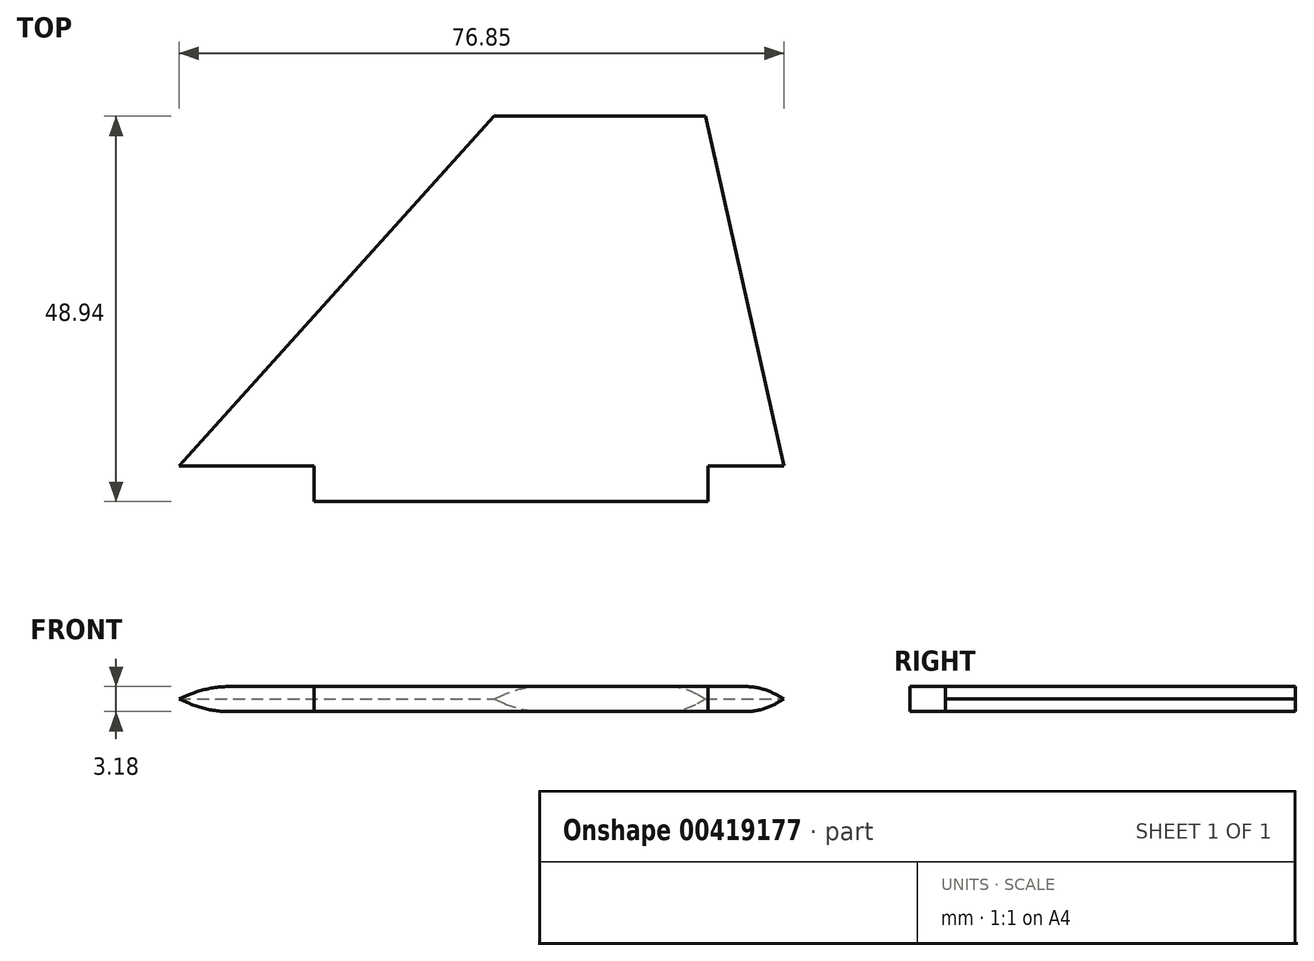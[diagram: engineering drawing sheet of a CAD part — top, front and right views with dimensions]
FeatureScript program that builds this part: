
annotation { "Feature Type Name" : "Feature", "Feature Type Description" : "" }
export const myFeature = defineFeature(function(context is Context, id is Id, definition is map)
    precondition{}
    {
        {
            var Q0;
            Q0=qCreatedBy(makeId("Top.planeOp"),FACE);
            var sketch = newSketch(context, id + "F0", { "sketchPlane" : qUnion([Q0])});
            skLineSegment(sketch, "E0", {"start": v(0, 0) * mm, "end": v(80, 0) * mm});
            skLineSegment(sketch, "E1", {"start": v(80, 0) * mm, "end": v(70, 44.44) * mm});
            skLineSegment(sketch, "E2", {"start": v(70, 44.44) * mm, "end": v(40, 44.44) * mm});
            skLineSegment(sketch, "E3", {"start": v(40, 44.44) * mm, "end": v(0, 0) * mm});
            skLineSegment(sketch, "E4", {"start": v(80, 0) * mm, "end": v(70, 0) * mm});
            skLineSegment(sketch, "E5", {"start": v(70, 0) * mm, "end": v(70, -4.5) * mm});
            skLineSegment(sketch, "E6", {"start": v(70, -4.5) * mm, "end": v(20, -4.5) * mm});
            skLineSegment(sketch, "E7", {"start": v(20, -4.5) * mm, "end": v(20, 0) * mm});
            skLineSegment(sketch, "E8", {"start": v(20, 0) * mm, "end": v(70, 0) * mm});
            skSolve(sketch);
        }
        {
            var Q0;
            Q0 = qSketchRegion(id + "F0", true);
            extrude(context, id + "F1", {"entities" : qUnion([Q0]), "endBound" : BoundingType.SYMMETRIC, "depth" : 3.17 * mm});
        }
        {
            var Q0;
            Q0=makeQuery(id+"F1.opExtrude","CAP_EDGE",EDGE,{"disambiguationData":[OSD([sQuery(id+"F0.wireOp",EDGE,"E3")])],"isStart":true});
            var Q1;
            Q1=makeQuery(id+"F1.opExtrude","CAP_EDGE",EDGE,{"disambiguationData":[OSD([sQuery(id+"F0.wireOp",EDGE,"E3")])],"isStart":false});
            chamfer(context, id + "F2", {"entities" : qUnion([Q0, Q1]), "chamferType" : ChamferType.OFFSET_ANGLE, "width" : 2.8 * mm, "oppositeDirection" : false, "angle" : 60 * degree, "tangentPropagation" : true});
        }
        {
            var Q0;
            Q0=makeQuery(id+"F1.opExtrude","CAP_EDGE",EDGE,{"disambiguationData":[OSD([sQuery(id+"F0.wireOp",EDGE,"E1")])],"isStart":true});
            var Q1;
            Q1=makeQuery(id+"F1.opExtrude","CAP_EDGE",EDGE,{"disambiguationData":[OSD([sQuery(id+"F0.wireOp",EDGE,"E1")])],"isStart":false});
            chamfer(context, id + "F3", {"entities" : qUnion([Q0, Q1]), "chamferType" : ChamferType.OFFSET_ANGLE, "width" : 1.78 * mm, "oppositeDirection" : false, "angle" : 60 * degree, "tangentPropagation" : true});
        }
        {
            var Q0;
            {var subQ0=sQuery(id+"F0.wireOp",EDGE,"E3");Q0=makeQuery(id+"F2.opChamfer","BLEND_EDGE",EDGE,{"blendedFrom":[makeQuery(id+"F1.opExtrude","CAP_EDGE",EDGE,{"disambiguationData":[OSD([subQ0])],"isStart":true}),makeQuery(id+"F1.opExtrude","CAP_FACE",FACE,{"disambiguationData":[OSD([sQuery(id+"F0.wireOp",EDGE,"E0"),sQuery(id+"F0.wireOp",EDGE,"E1"),sQuery(id+"F0.wireOp",EDGE,"E2"),subQ0,sQuery(id+"F0.wireOp",EDGE,"E4"),sQuery(id+"F0.wireOp",EDGE,"E5"),sQuery(id+"F0.wireOp",EDGE,"E6"),sQuery(id+"F0.wireOp",EDGE,"E7")])],"isStart":true})],"blendedInto":[makeQuery(id+"F1.opExtrude","CAP_FACE",FACE,{"disambiguationData":[OSD([sQuery(id+"F0.wireOp",EDGE,"E0"),sQuery(id+"F0.wireOp",EDGE,"E1"),sQuery(id+"F0.wireOp",EDGE,"E2"),subQ0,sQuery(id+"F0.wireOp",EDGE,"E4"),sQuery(id+"F0.wireOp",EDGE,"E5"),sQuery(id+"F0.wireOp",EDGE,"E6"),sQuery(id+"F0.wireOp",EDGE,"E7")])],"isStart":true})]});}
            var Q1;
            {var subQ0=sQuery(id+"F0.wireOp",EDGE,"E1");Q1=makeQuery(id+"F3.opChamfer","BLEND_EDGE",EDGE,{"blendedFrom":[makeQuery(id+"F1.opExtrude","CAP_EDGE",EDGE,{"disambiguationData":[OSD([subQ0])],"isStart":true}),makeQuery(id+"F1.opExtrude","CAP_FACE",FACE,{"disambiguationData":[OSD([sQuery(id+"F0.wireOp",EDGE,"E0"),subQ0,sQuery(id+"F0.wireOp",EDGE,"E2"),sQuery(id+"F0.wireOp",EDGE,"E3"),sQuery(id+"F0.wireOp",EDGE,"E4"),sQuery(id+"F0.wireOp",EDGE,"E5"),sQuery(id+"F0.wireOp",EDGE,"E6"),sQuery(id+"F0.wireOp",EDGE,"E7")])],"isStart":true})],"blendedInto":[makeQuery(id+"F1.opExtrude","CAP_FACE",FACE,{"disambiguationData":[OSD([sQuery(id+"F0.wireOp",EDGE,"E0"),subQ0,sQuery(id+"F0.wireOp",EDGE,"E2"),sQuery(id+"F0.wireOp",EDGE,"E3"),sQuery(id+"F0.wireOp",EDGE,"E4"),sQuery(id+"F0.wireOp",EDGE,"E5"),sQuery(id+"F0.wireOp",EDGE,"E6"),sQuery(id+"F0.wireOp",EDGE,"E7")])],"isStart":true})]});}
            var Q2;
            {var subQ0=sQuery(id+"F0.wireOp",EDGE,"E1");Q2=makeQuery(id+"F3.opChamfer","BLEND_EDGE",EDGE,{"blendedFrom":[makeQuery(id+"F1.opExtrude","CAP_EDGE",EDGE,{"disambiguationData":[OSD([subQ0])],"isStart":false}),makeQuery(id+"F1.opExtrude","CAP_FACE",FACE,{"disambiguationData":[OSD([sQuery(id+"F0.wireOp",EDGE,"E0"),subQ0,sQuery(id+"F0.wireOp",EDGE,"E2"),sQuery(id+"F0.wireOp",EDGE,"E3"),sQuery(id+"F0.wireOp",EDGE,"E4"),sQuery(id+"F0.wireOp",EDGE,"E5"),sQuery(id+"F0.wireOp",EDGE,"E6"),sQuery(id+"F0.wireOp",EDGE,"E7")])],"isStart":false})],"blendedInto":[makeQuery(id+"F1.opExtrude","CAP_FACE",FACE,{"disambiguationData":[OSD([sQuery(id+"F0.wireOp",EDGE,"E0"),subQ0,sQuery(id+"F0.wireOp",EDGE,"E2"),sQuery(id+"F0.wireOp",EDGE,"E3"),sQuery(id+"F0.wireOp",EDGE,"E4"),sQuery(id+"F0.wireOp",EDGE,"E5"),sQuery(id+"F0.wireOp",EDGE,"E6"),sQuery(id+"F0.wireOp",EDGE,"E7")])],"isStart":false})]});}
            var Q3;
            {var subQ0=sQuery(id+"F0.wireOp",EDGE,"E3");Q3=makeQuery(id+"F2.opChamfer","BLEND_EDGE",EDGE,{"blendedFrom":[makeQuery(id+"F1.opExtrude","CAP_EDGE",EDGE,{"disambiguationData":[OSD([subQ0])],"isStart":false}),makeQuery(id+"F1.opExtrude","CAP_FACE",FACE,{"disambiguationData":[OSD([sQuery(id+"F0.wireOp",EDGE,"E0"),sQuery(id+"F0.wireOp",EDGE,"E1"),sQuery(id+"F0.wireOp",EDGE,"E2"),subQ0,sQuery(id+"F0.wireOp",EDGE,"E4"),sQuery(id+"F0.wireOp",EDGE,"E5"),sQuery(id+"F0.wireOp",EDGE,"E6"),sQuery(id+"F0.wireOp",EDGE,"E7")])],"isStart":false})],"blendedInto":[makeQuery(id+"F1.opExtrude","CAP_FACE",FACE,{"disambiguationData":[OSD([sQuery(id+"F0.wireOp",EDGE,"E0"),sQuery(id+"F0.wireOp",EDGE,"E1"),sQuery(id+"F0.wireOp",EDGE,"E2"),subQ0,sQuery(id+"F0.wireOp",EDGE,"E4"),sQuery(id+"F0.wireOp",EDGE,"E5"),sQuery(id+"F0.wireOp",EDGE,"E6"),sQuery(id+"F0.wireOp",EDGE,"E7")])],"isStart":false})]});}
            fillet(context, id + "F4", {"entities" : qUnion([Q0, Q1, Q2, Q3]), "radius" : 7.62 * mm, "tangentPropagation" : true, "allowEdgeOverflow" : false});
        }
    });
